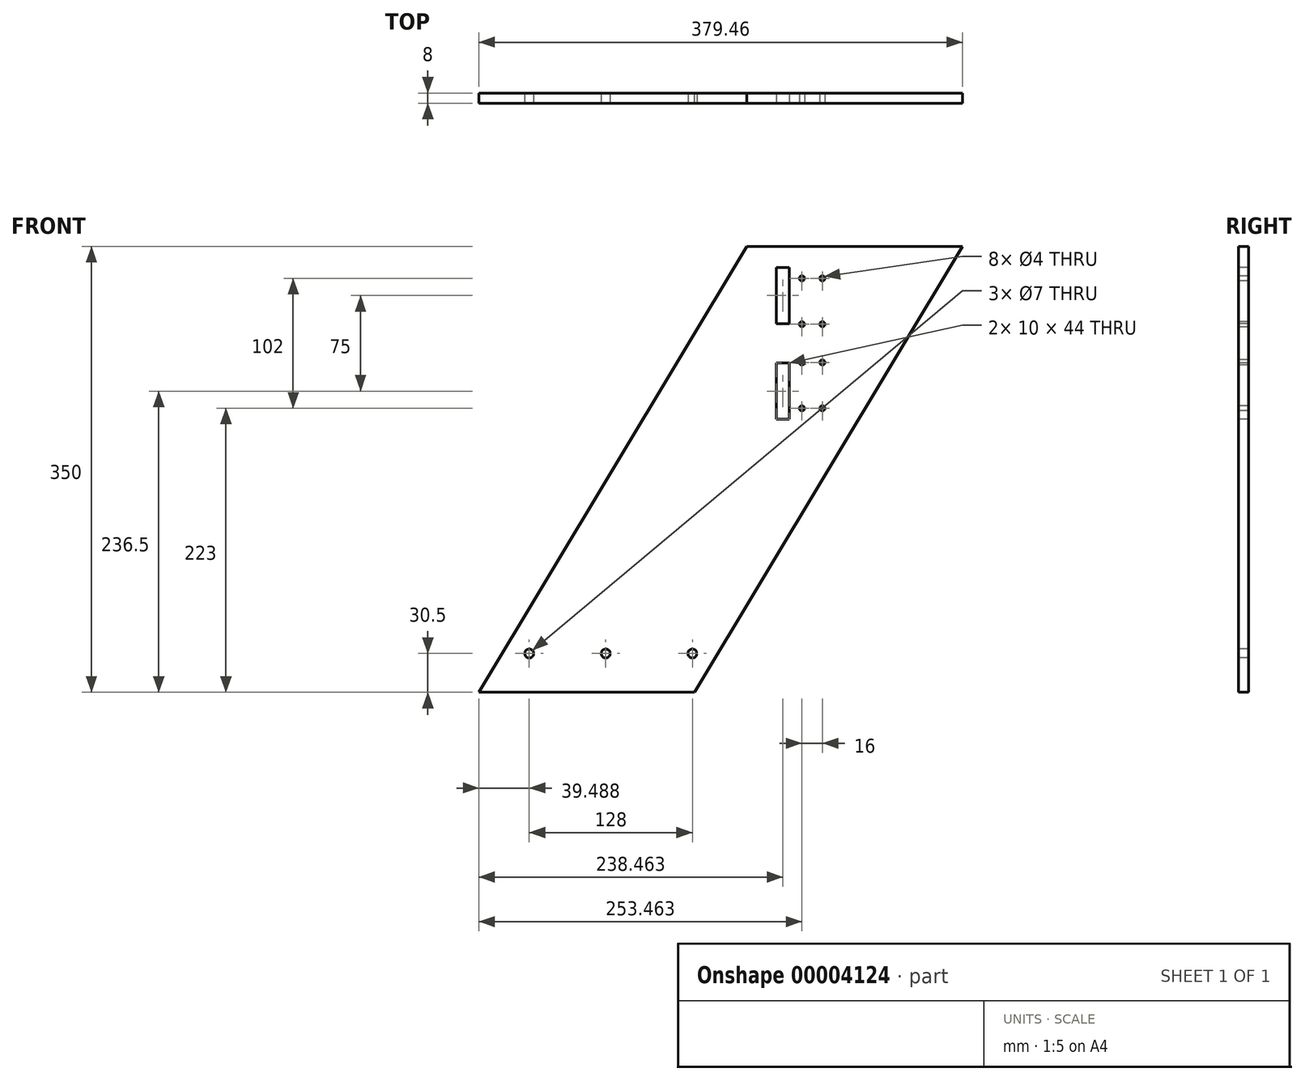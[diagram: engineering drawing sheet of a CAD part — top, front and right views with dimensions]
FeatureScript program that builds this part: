
annotation { "Feature Type Name" : "Feature", "Feature Type Description" : "" }
export const myFeature = defineFeature(function(context is Context, id is Id, definition is map)
    precondition{}
    {
        {
            var Q0;
            Q0=qCreatedBy(makeId("Front.planeOp"),FACE);
            var sketch = newSketch(context, id + "F0", { "sketchPlane" : qUnion([Q0])});
            skLineSegment(sketch, "E0", {"start": v(0, 0) * mm, "end": v(169.16, 0) * mm});
            skLineSegment(sketch, "E1", {"start": v(169.16, 0) * mm, "end": v(379.46, 350) * mm});
            skLineSegment(sketch, "E2", {"start": v(0, 0) * mm, "end": v(210.3, 350) * mm});
            skLineSegment(sketch, "E3", {"start": v(210.3, 350) * mm, "end": v(379.46, 350) * mm});
            skSolve(sketch);
        }
        {
            var Q0;
            Q0=makeQuery(id+"F0.imprint","IMPRINT",FACE,{"disambiguationData":[TD([[makeQuery(id+"F0.imprint","IMPRINT",EDGE,{"derivedFrom":sQuery(id+"F0.wireOp",EDGE,"E0")}),1.0]])]});
            extrude(context, id + "F1", {"entities" : qUnion([Q0]), "depth" : 8 * mm});
        }
        {
            var Q0;
            Q0=makeQuery(id+"F1.opExtrude","CAP_FACE",FACE,{"disambiguationData":[OSD([sQuery(id+"F0.wireOp",EDGE,"E0"),sQuery(id+"F0.wireOp",EDGE,"E1"),sQuery(id+"F0.wireOp",EDGE,"E2"),sQuery(id+"F0.wireOp",EDGE,"E3")])],"isStart":false});
            var sketch = newSketch(context, id + "F2", { "sketchPlane" : qUnion([Q0])});
            skLineSegment(sketch, "E4", {"start": v(212.54, 30.5) * mm, "end": v(-13.56, 30.5) * mm});
            skCircle(sketch, "E5", {"center": v(39.49, 30.5) * mm, "radius": 3.5 * mm});
            skLineSegment(sketch, "E6", {"start": v(187.49, 30.5) * mm, "end": v(187.49, 0) * mm});
            skCircle(sketch, "E7", {"center": v(167.49, 30.5) * mm, "radius": 3.5 * mm});
            skLineSegment(sketch, "E8", {"start": v(18.33, 30.5) * mm, "end": v(18.33, 0) * mm});
            skCircle(sketch, "E9", {"center": v(99.49, 30.5) * mm, "radius": 3.5 * mm});
            skSolve(sketch);
        }
        {
            var Q0;
            {var subQ0=sQuery(id+"F2.wireOp",EDGE,"E5");var subQ1=sQuery(id+"F2.wireOp",EDGE,"E4");var subQ3=makeQuery(id+"F2.imprint","INTERSECT",VERTEX,{"disambiguationData":[OD(0.0)],"derivedFrom":[subQ1,subQ0]});Q0=makeQuery(id+"F2.imprint","IMPRINT",FACE,{"disambiguationData":[TD([[makeQuery(id+"F2.imprint","IMPRINT",EDGE,{"disambiguationData":[TD([[subQ3,-1.0]])],"derivedFrom":subQ1}),1.0]])]});}
            var Q1;
            {var subQ0=sQuery(id+"F2.wireOp",EDGE,"E5");var subQ1=sQuery(id+"F2.wireOp",EDGE,"E4");var subQ3=makeQuery(id+"F2.imprint","INTERSECT",VERTEX,{"disambiguationData":[OD(0.0)],"derivedFrom":[subQ1,subQ0]});Q1=makeQuery(id+"F2.imprint","IMPRINT",FACE,{"disambiguationData":[TD([[makeQuery(id+"F2.imprint","IMPRINT",EDGE,{"disambiguationData":[TD([[subQ3,-1.0]])],"derivedFrom":subQ1}),-1.0]])]});}
            var Q2;
            {var subQ0=sQuery(id+"F2.wireOp",EDGE,"E7");var subQ1=sQuery(id+"F2.wireOp",EDGE,"E4");var subQ3=makeQuery(id+"F2.imprint","INTERSECT",VERTEX,{"disambiguationData":[OD(0.0)],"derivedFrom":[subQ1,subQ0]});Q2=makeQuery(id+"F2.imprint","IMPRINT",FACE,{"disambiguationData":[TD([[makeQuery(id+"F2.imprint","IMPRINT",EDGE,{"disambiguationData":[TD([[subQ3,-1.0]])],"derivedFrom":subQ1}),1.0]])]});}
            var Q3;
            {var subQ0=sQuery(id+"F2.wireOp",EDGE,"E7");var subQ1=sQuery(id+"F2.wireOp",EDGE,"E4");var subQ3=makeQuery(id+"F2.imprint","INTERSECT",VERTEX,{"disambiguationData":[OD(0.0)],"derivedFrom":[subQ1,subQ0]});Q3=makeQuery(id+"F2.imprint","IMPRINT",FACE,{"disambiguationData":[TD([[makeQuery(id+"F2.imprint","IMPRINT",EDGE,{"disambiguationData":[TD([[subQ3,-1.0]])],"derivedFrom":subQ1}),-1.0]])]});}
            var Q4;
            {var subQ0=sQuery(id+"F2.wireOp",EDGE,"E9");var subQ1=sQuery(id+"F2.wireOp",EDGE,"E4");var subQ3=makeQuery(id+"F2.imprint","INTERSECT",VERTEX,{"disambiguationData":[OD(0.0)],"derivedFrom":[subQ1,subQ0]});Q4=makeQuery(id+"F2.imprint","IMPRINT",FACE,{"disambiguationData":[TD([[makeQuery(id+"F2.imprint","IMPRINT",EDGE,{"disambiguationData":[TD([[subQ3,-1.0]])],"derivedFrom":subQ1}),1.0]])]});}
            var Q5;
            {var subQ0=sQuery(id+"F2.wireOp",EDGE,"E9");var subQ1=sQuery(id+"F2.wireOp",EDGE,"E4");var subQ3=makeQuery(id+"F2.imprint","INTERSECT",VERTEX,{"disambiguationData":[OD(0.0)],"derivedFrom":[subQ1,subQ0]});Q5=makeQuery(id+"F2.imprint","IMPRINT",FACE,{"disambiguationData":[TD([[makeQuery(id+"F2.imprint","IMPRINT",EDGE,{"disambiguationData":[TD([[subQ3,-1.0]])],"derivedFrom":subQ1}),-1.0]])]});}
            extrude(context, id + "F3", {"entities" : qUnion([Q0, Q1, Q2, Q3, Q4, Q5]), "operationType" : NewBodyOperationType.REMOVE, "oppositeDirection" : true, "depth" : 25 * mm});
        }
        {
            var Q0;
            Q0=makeQuery(id+"F1.opExtrude","CAP_FACE",FACE,{"disambiguationData":[OSD([sQuery(id+"F0.wireOp",EDGE,"E0"),sQuery(id+"F0.wireOp",EDGE,"E1"),sQuery(id+"F0.wireOp",EDGE,"E2"),sQuery(id+"F0.wireOp",EDGE,"E3")])],"isStart":false});
            var sketch = newSketch(context, id + "F4", { "sketchPlane" : qUnion([Q0])});
            skLineSegment(sketch, "E10.bottom", {"start": v(253.46, 325) * mm, "end": v(269.46, 325) * mm});
            skLineSegment(sketch, "E10.top", {"start": v(253.46, 289) * mm, "end": v(269.46, 289) * mm});
            skLineSegment(sketch, "E10.left", {"start": v(253.46, 325) * mm, "end": v(253.46, 289) * mm});
            skLineSegment(sketch, "E10.right", {"start": v(269.46, 325) * mm, "end": v(269.46, 289) * mm});
            skLineSegment(sketch, "E11.bottom", {"start": v(253.46, 259) * mm, "end": v(269.46, 259) * mm});
            skLineSegment(sketch, "E11.top", {"start": v(253.46, 223) * mm, "end": v(269.46, 223) * mm});
            skLineSegment(sketch, "E11.left", {"start": v(253.46, 259) * mm, "end": v(253.46, 223) * mm});
            skLineSegment(sketch, "E11.right", {"start": v(269.46, 259) * mm, "end": v(269.46, 223) * mm});
            skCircle(sketch, "E12", {"center": v(253.46, 325) * mm, "radius": 2 * mm});
            skCircle(sketch, "E13", {"center": v(269.46, 325) * mm, "radius": 2 * mm});
            skCircle(sketch, "E14", {"center": v(253.46, 289) * mm, "radius": 2 * mm});
            skCircle(sketch, "E15", {"center": v(269.46, 289) * mm, "radius": 2 * mm});
            skCircle(sketch, "E16", {"center": v(253.46, 259) * mm, "radius": 2 * mm});
            skCircle(sketch, "E17", {"center": v(269.46, 259) * mm, "radius": 2 * mm});
            skCircle(sketch, "E18", {"center": v(253.46, 223) * mm, "radius": 2 * mm});
            skCircle(sketch, "E19", {"center": v(269.46, 223) * mm, "radius": 2 * mm});
            skSolve(sketch);
        }
        {
            var Q0;
            {var subQ1=sQuery(id+"F4.wireOp",EDGE,"E10.left");var subQ3=sQuery(id+"F4.wireOp",EDGE,"E10.bottom");var subQ5=makeQuery(id+"F4.imprint","INTERSECT",VERTEX,{"derivedFrom":[subQ3,subQ1]});Q0=makeQuery(id+"F4.imprint","IMPRINT",FACE,{"disambiguationData":[TD([[makeQuery(id+"F4.imprint","IMPRINT",EDGE,{"disambiguationData":[TD([[subQ5,-1.0]])],"derivedFrom":subQ3}),1.0]])]});}
            var Q1;
            {var subQ1=sQuery(id+"F4.wireOp",EDGE,"E10.left");var subQ3=sQuery(id+"F4.wireOp",EDGE,"E10.bottom");var subQ5=makeQuery(id+"F4.imprint","INTERSECT",VERTEX,{"derivedFrom":[subQ3,subQ1]});Q1=makeQuery(id+"F4.imprint","IMPRINT",FACE,{"disambiguationData":[TD([[makeQuery(id+"F4.imprint","IMPRINT",EDGE,{"disambiguationData":[TD([[subQ5,-1.0]])],"derivedFrom":subQ3}),-1.0]])]});}
            var Q2;
            {var subQ1=sQuery(id+"F4.wireOp",EDGE,"E10.left");var subQ3=sQuery(id+"F4.wireOp",EDGE,"E10.top");var subQ5=makeQuery(id+"F4.imprint","INTERSECT",VERTEX,{"derivedFrom":[subQ3,subQ1]});Q2=makeQuery(id+"F4.imprint","IMPRINT",FACE,{"disambiguationData":[TD([[makeQuery(id+"F4.imprint","IMPRINT",EDGE,{"disambiguationData":[TD([[subQ5,-1.0]])],"derivedFrom":subQ3}),-1.0]])]});}
            var Q3;
            {var subQ1=sQuery(id+"F4.wireOp",EDGE,"E10.left");var subQ3=sQuery(id+"F4.wireOp",EDGE,"E10.top");var subQ5=makeQuery(id+"F4.imprint","INTERSECT",VERTEX,{"derivedFrom":[subQ3,subQ1]});Q3=makeQuery(id+"F4.imprint","IMPRINT",FACE,{"disambiguationData":[TD([[makeQuery(id+"F4.imprint","IMPRINT",EDGE,{"disambiguationData":[TD([[subQ5,-1.0]])],"derivedFrom":subQ3}),1.0]])]});}
            var Q4;
            {var subQ1=sQuery(id+"F4.wireOp",EDGE,"E10.right");var subQ3=sQuery(id+"F4.wireOp",EDGE,"E10.top");var subQ5=makeQuery(id+"F4.imprint","INTERSECT",VERTEX,{"derivedFrom":[subQ3,subQ1]});Q4=makeQuery(id+"F4.imprint","IMPRINT",FACE,{"disambiguationData":[TD([[makeQuery(id+"F4.imprint","IMPRINT",EDGE,{"disambiguationData":[TD([[subQ5,1.0]])],"derivedFrom":subQ3}),1.0]])]});}
            var Q5;
            {var subQ1=sQuery(id+"F4.wireOp",EDGE,"E10.right");var subQ3=sQuery(id+"F4.wireOp",EDGE,"E10.top");var subQ5=makeQuery(id+"F4.imprint","INTERSECT",VERTEX,{"derivedFrom":[subQ3,subQ1]});Q5=makeQuery(id+"F4.imprint","IMPRINT",FACE,{"disambiguationData":[TD([[makeQuery(id+"F4.imprint","IMPRINT",EDGE,{"disambiguationData":[TD([[subQ5,1.0]])],"derivedFrom":subQ3}),-1.0]])]});}
            var Q6;
            {var subQ1=sQuery(id+"F4.wireOp",EDGE,"E10.right");var subQ3=sQuery(id+"F4.wireOp",EDGE,"E10.bottom");var subQ5=makeQuery(id+"F4.imprint","INTERSECT",VERTEX,{"derivedFrom":[subQ3,subQ1]});Q6=makeQuery(id+"F4.imprint","IMPRINT",FACE,{"disambiguationData":[TD([[makeQuery(id+"F4.imprint","IMPRINT",EDGE,{"disambiguationData":[TD([[subQ5,1.0]])],"derivedFrom":subQ3}),-1.0]])]});}
            var Q7;
            {var subQ1=sQuery(id+"F4.wireOp",EDGE,"E10.right");var subQ3=sQuery(id+"F4.wireOp",EDGE,"E10.bottom");var subQ5=makeQuery(id+"F4.imprint","INTERSECT",VERTEX,{"derivedFrom":[subQ3,subQ1]});Q7=makeQuery(id+"F4.imprint","IMPRINT",FACE,{"disambiguationData":[TD([[makeQuery(id+"F4.imprint","IMPRINT",EDGE,{"disambiguationData":[TD([[subQ5,1.0]])],"derivedFrom":subQ3}),1.0]])]});}
            var Q8;
            {var subQ1=sQuery(id+"F4.wireOp",EDGE,"E11.left");var subQ3=sQuery(id+"F4.wireOp",EDGE,"E11.top");var subQ5=makeQuery(id+"F4.imprint","INTERSECT",VERTEX,{"derivedFrom":[subQ3,subQ1]});Q8=makeQuery(id+"F4.imprint","IMPRINT",FACE,{"disambiguationData":[TD([[makeQuery(id+"F4.imprint","IMPRINT",EDGE,{"disambiguationData":[TD([[subQ5,-1.0]])],"derivedFrom":subQ3}),1.0]])]});}
            var Q9;
            {var subQ1=sQuery(id+"F4.wireOp",EDGE,"E11.left");var subQ3=sQuery(id+"F4.wireOp",EDGE,"E11.top");var subQ5=makeQuery(id+"F4.imprint","INTERSECT",VERTEX,{"derivedFrom":[subQ3,subQ1]});Q9=makeQuery(id+"F4.imprint","IMPRINT",FACE,{"disambiguationData":[TD([[makeQuery(id+"F4.imprint","IMPRINT",EDGE,{"disambiguationData":[TD([[subQ5,-1.0]])],"derivedFrom":subQ3}),-1.0]])]});}
            var Q10;
            {var subQ1=sQuery(id+"F4.wireOp",EDGE,"E11.right");var subQ3=sQuery(id+"F4.wireOp",EDGE,"E11.top");var subQ5=makeQuery(id+"F4.imprint","INTERSECT",VERTEX,{"derivedFrom":[subQ3,subQ1]});Q10=makeQuery(id+"F4.imprint","IMPRINT",FACE,{"disambiguationData":[TD([[makeQuery(id+"F4.imprint","IMPRINT",EDGE,{"disambiguationData":[TD([[subQ5,1.0]])],"derivedFrom":subQ3}),1.0]])]});}
            var Q11;
            {var subQ1=sQuery(id+"F4.wireOp",EDGE,"E11.right");var subQ3=sQuery(id+"F4.wireOp",EDGE,"E11.top");var subQ5=makeQuery(id+"F4.imprint","INTERSECT",VERTEX,{"derivedFrom":[subQ3,subQ1]});Q11=makeQuery(id+"F4.imprint","IMPRINT",FACE,{"disambiguationData":[TD([[makeQuery(id+"F4.imprint","IMPRINT",EDGE,{"disambiguationData":[TD([[subQ5,1.0]])],"derivedFrom":subQ3}),-1.0]])]});}
            var Q12;
            {var subQ1=sQuery(id+"F4.wireOp",EDGE,"E11.right");var subQ3=sQuery(id+"F4.wireOp",EDGE,"E11.bottom");var subQ5=makeQuery(id+"F4.imprint","INTERSECT",VERTEX,{"derivedFrom":[subQ3,subQ1]});Q12=makeQuery(id+"F4.imprint","IMPRINT",FACE,{"disambiguationData":[TD([[makeQuery(id+"F4.imprint","IMPRINT",EDGE,{"disambiguationData":[TD([[subQ5,1.0]])],"derivedFrom":subQ3}),-1.0]])]});}
            var Q13;
            {var subQ0=sQuery(id+"F4.wireOp",EDGE,"E11.right");var subQ3=sQuery(id+"F4.wireOp",EDGE,"E11.bottom");var subQ4=makeQuery(id+"F4.imprint","INTERSECT",VERTEX,{"derivedFrom":[subQ3,subQ0]});Q13=makeQuery(id+"F4.imprint","IMPRINT",FACE,{"disambiguationData":[TD([[makeQuery(id+"F4.imprint","IMPRINT",EDGE,{"disambiguationData":[TD([[subQ4,1.0]])],"derivedFrom":subQ3}),1.0]])]});}
            var Q14;
            {var subQ1=sQuery(id+"F4.wireOp",EDGE,"E11.left");var subQ3=sQuery(id+"F4.wireOp",EDGE,"E11.bottom");var subQ5=makeQuery(id+"F4.imprint","INTERSECT",VERTEX,{"derivedFrom":[subQ3,subQ1]});Q14=makeQuery(id+"F4.imprint","IMPRINT",FACE,{"disambiguationData":[TD([[makeQuery(id+"F4.imprint","IMPRINT",EDGE,{"disambiguationData":[TD([[subQ5,-1.0]])],"derivedFrom":subQ3}),-1.0]])]});}
            var Q15;
            {var subQ1=sQuery(id+"F4.wireOp",EDGE,"E11.left");var subQ3=sQuery(id+"F4.wireOp",EDGE,"E11.bottom");var subQ5=makeQuery(id+"F4.imprint","INTERSECT",VERTEX,{"derivedFrom":[subQ3,subQ1]});Q15=makeQuery(id+"F4.imprint","IMPRINT",FACE,{"disambiguationData":[TD([[makeQuery(id+"F4.imprint","IMPRINT",EDGE,{"disambiguationData":[TD([[subQ5,-1.0]])],"derivedFrom":subQ3}),1.0]])]});}
            extrude(context, id + "F5", {"entities" : qUnion([Q0, Q1, Q2, Q3, Q4, Q5, Q6, Q7, Q8, Q9, Q10, Q11, Q12, Q13, Q14, Q15]), "operationType" : NewBodyOperationType.REMOVE, "oppositeDirection" : true, "depth" : 25 * mm});
        }
        {
            var Q0;
            Q0=makeQuery(id+"F1.opExtrude","CAP_FACE",FACE,{"disambiguationData":[OSD([sQuery(id+"F0.wireOp",EDGE,"E0"),sQuery(id+"F0.wireOp",EDGE,"E1"),sQuery(id+"F0.wireOp",EDGE,"E2"),sQuery(id+"F0.wireOp",EDGE,"E3")])],"isStart":false});
            var sketch = newSketch(context, id + "F6", { "sketchPlane" : qUnion([Q0])});
            skLineSegment(sketch, "E20", {"start": v(253.46, 236.5) * mm, "end": v(228.56, 236.5) * mm});
            skLineSegment(sketch, "E21", {"start": v(243.46, 236.5) * mm, "end": v(243.46, 214.5) * mm});
            skLineSegment(sketch, "E22", {"start": v(243.46, 214.5) * mm, "end": v(233.46, 214.5) * mm});
            skLineSegment(sketch, "E23", {"start": v(233.46, 214.5) * mm, "end": v(233.46, 236.5) * mm});
            skLineSegment(sketch, "E24.0.MirrorCS", {"start": v(233.46, 258.5) * mm, "end": v(233.46, 236.5) * mm});
            skLineSegment(sketch, "E25.0.MirrorCS", {"start": v(243.46, 236.5) * mm, "end": v(243.46, 258.5) * mm});
            skLineSegment(sketch, "E26.0.MirrorCS", {"start": v(243.46, 258.5) * mm, "end": v(233.46, 258.5) * mm});
            skLineSegment(sketch, "E27", {"start": v(253.46, 259) * mm, "end": v(253.46, 223) * mm});
            skLineSegment(sketch, "E28", {"start": v(237.68, 311.5) * mm, "end": v(295.14, 311.5) * mm});
            skLineSegment(sketch, "E29", {"start": v(253.46, 325) * mm, "end": v(253.46, 289) * mm});
            skLineSegment(sketch, "E30", {"start": v(243.46, 311.5) * mm, "end": v(243.46, 333.5) * mm});
            skLineSegment(sketch, "E31", {"start": v(243.46, 333.5) * mm, "end": v(233.46, 333.5) * mm});
            skLineSegment(sketch, "E32", {"start": v(233.46, 333.5) * mm, "end": v(233.46, 311.5) * mm});
            skLineSegment(sketch, "E33.0.MirrorCS", {"start": v(243.46, 311.5) * mm, "end": v(243.46, 289.5) * mm});
            skLineSegment(sketch, "E34.0.MirrorCS", {"start": v(233.46, 289.5) * mm, "end": v(233.46, 311.5) * mm});
            skLineSegment(sketch, "E35.0.MirrorCS", {"start": v(243.46, 289.5) * mm, "end": v(233.46, 289.5) * mm});
            skSolve(sketch);
        }
        {
            var Q0;
            {var subQ1=sQuery(id+"F6.wireOp",EDGE,"E21");Q0=makeQuery(id+"F6.imprint","IMPRINT",FACE,{"disambiguationData":[TD([[makeQuery(id+"F6.imprint","IMPRINT",EDGE,{"derivedFrom":subQ1}),-1.0]])]});}
            var Q1;
            {var subQ0=sQuery(id+"F6.wireOp",EDGE,"E24.0.MirrorCS");Q1=makeQuery(id+"F6.imprint","IMPRINT",FACE,{"disambiguationData":[TD([[makeQuery(id+"F6.imprint","IMPRINT",EDGE,{"derivedFrom":subQ0}),1.0]])]});}
            var Q2;
            {var subQ1=sQuery(id+"F6.wireOp",EDGE,"E33.0.MirrorCS");Q2=makeQuery(id+"F6.imprint","IMPRINT",FACE,{"disambiguationData":[TD([[makeQuery(id+"F6.imprint","IMPRINT",EDGE,{"derivedFrom":subQ1}),-1.0]])]});}
            var Q3;
            {var subQ1=sQuery(id+"F6.wireOp",EDGE,"E30");Q3=makeQuery(id+"F6.imprint","IMPRINT",FACE,{"disambiguationData":[TD([[makeQuery(id+"F6.imprint","IMPRINT",EDGE,{"derivedFrom":subQ1}),1.0]])]});}
            extrude(context, id + "F7", {"entities" : qUnion([Q0, Q1, Q2, Q3]), "operationType" : NewBodyOperationType.REMOVE, "oppositeDirection" : true, "depth" : 25 * mm});
        }
    });
